# Revit family: Haworth_X99_Seminar_Chair_AP_PRELIMINARY
name_source: partatom
category: Furniture
revit_build: Autodesk Revit 2018 (Build: 20170223_1515(x64)
units: mm (PartAtom-declared; Revit-internal decimal feet)

## family parameters
Always vertical = Yes
Cut with Voids When Loaded = No
OmniClass Number = 23.40.70.14.64.11
OmniClass Title = Office Furniture
Room Calculation Point = No
Shared = No
Work Plane-Based = No

## types (3) — shared parameters
Aluminum Base = Yes
Assembly Code = E2020200
Base Finish = Haworth _ Metal _ Chrome
Description = Haworth - X99 - Chair - Seminar
Manufacturer = Haworth
Model = SE99GMXX
Nested Base = Yes
Revision Number = 2
Size = Verify Final Dim. w/Haworth
Steel Base = No
URL = https://www.haworth.com
URL - Product = https://www.haworth.com
Warranty = http://www.haworth.com

## per-type parameters (varying)
| type | Arm Armless | Arms Fixed | Back Mesh | Casters | Glides |
| Mesh Back | No | Yes | Yes | Yes | No |
| Back Cushion | No | Yes | No | No | Yes |
| Armless | Yes | No | No | Yes | No |

type visibility flags (boolean, named after types; folded from table):
- Mesh Back: Yes: (none)
- Back Cushion: Yes: Back Cushion
- Armless: Yes: Back Cushion

## geometry (parser evidence)
native form markers: Sweep x11
no freeform markers — native parametric forms only
